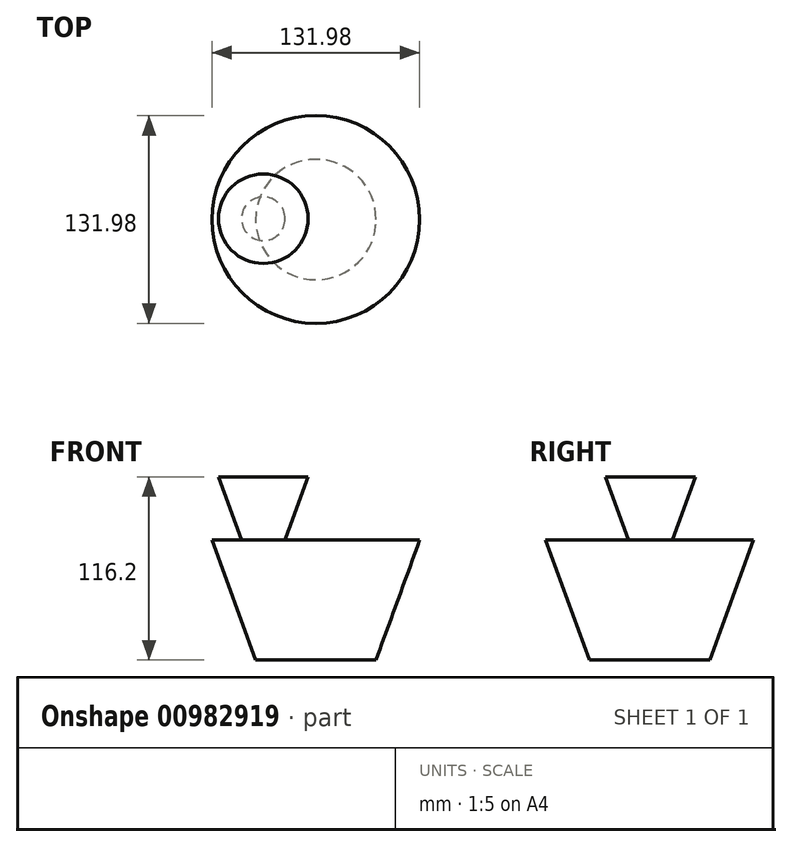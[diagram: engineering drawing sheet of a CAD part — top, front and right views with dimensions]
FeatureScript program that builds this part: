
annotation { "Feature Type Name" : "Feature", "Feature Type Description" : "" }
export const myFeature = defineFeature(function(context is Context, id is Id, definition is map)
    precondition{}
    {
        {
            var Q0;
            Q0=qCreatedBy(makeId("Top.planeOp"),FACE);
            var sketch = newSketch(context, id + "F0", { "sketchPlane" : qUnion([Q0])});
            skCircle(sketch, "E0", {"center": v(-3.06, 2.57) * mm, "radius": 38.26 * mm});
            skSolve(sketch);
        }
        {
            var Q0;
            Q0 = qSketchRegion(id + "F0", true);
            extrude(context, id + "F1", {"entities" : qUnion([Q0]), "depth" : 76.2 * mm, "offsetDistance" : 25.4 * mm, "hasDraft" : true, "draftAngle" : 20 * degree});
        }
        {
            var Q0;
            Q0=makeQuery(id+"F1.opExtrude","CAP_FACE",FACE,{"disambiguationData":[OSD([sQuery(id+"F0.wireOp",EDGE,"E0")])],"isStart":false});
            var sketch = newSketch(context, id + "F2", { "sketchPlane" : qUnion([Q0])});
            skCircle(sketch, "E1", {"center": v(-36.42, 3.1) * mm, "radius": 13.89 * mm});
            skSolve(sketch);
        }
        {
            var Q0;
            Q0=makeQuery(id+"F2.imprint","IMPRINT",FACE,{"disambiguationData":[TD([[makeQuery(id+"F2.imprint","IMPRINT",EDGE,{"derivedFrom":sQuery(id+"F2.wireOp",EDGE,"E1")}),1.0]])]});
            extrude(context, id + "F3", {"entities" : qUnion([Q0]), "operationType" : NewBodyOperationType.ADD, "depth" : 40 * mm, "offsetDistance" : 25 * mm, "hasDraft" : true, "draftAngle" : 20 * degree});
        }
    });
